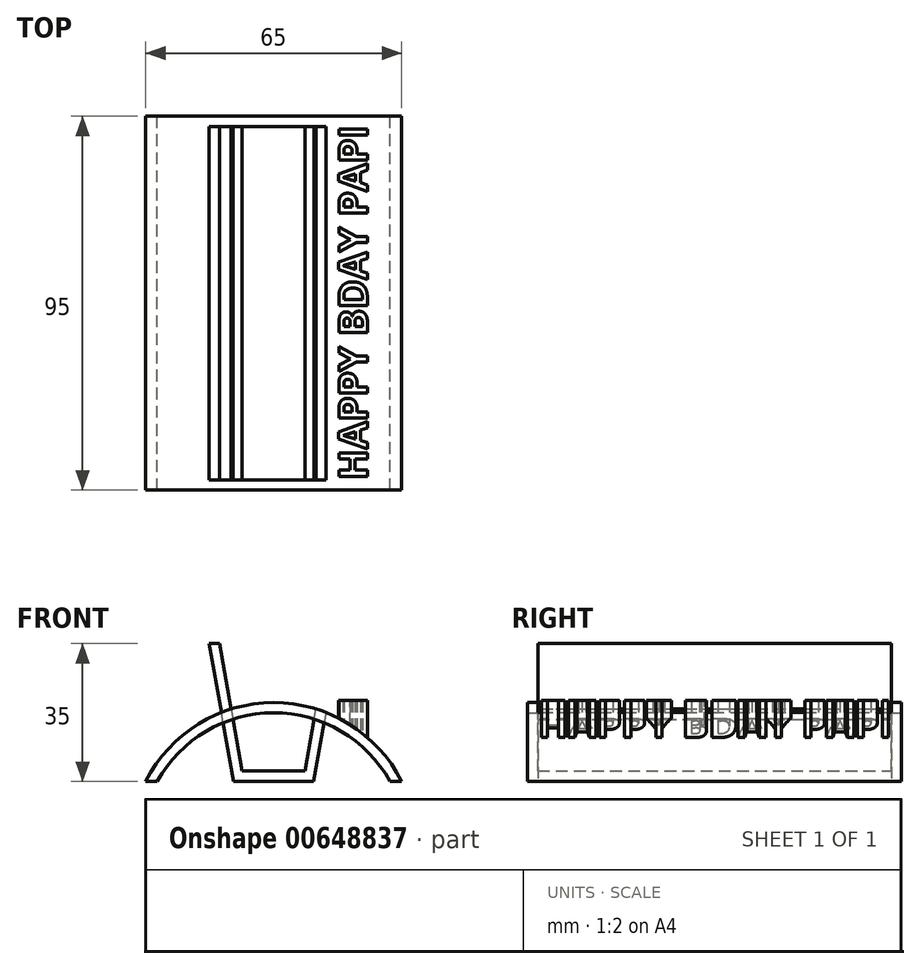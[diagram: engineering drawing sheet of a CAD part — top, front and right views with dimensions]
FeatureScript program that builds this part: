
annotation { "Feature Type Name" : "Feature", "Feature Type Description" : "" }
export const myFeature = defineFeature(function(context is Context, id is Id, definition is map)
    precondition{}
    {
        {
            var Q0;
            Q0=qCreatedBy(makeId("Front.planeOp"),FACE);
            var sketch = newSketch(context, id + "F0", { "sketchPlane" : qUnion([Q0])});
            skArc(sketch, "E0", {"start": v(32.5, 0) * mm, "mid": v(0, 20) * mm, "end": v(-32.5, 0) * mm});
            skLineSegment(sketch, "E1", {"start": v(-32.5, 0) * mm, "end": v(-29.56, 0) * mm});
            skArc(sketch, "E2", {"start": v(29.56, 0) * mm, "mid": v(0, 17.4) * mm, "end": v(-29.56, 0) * mm});
            skLineSegment(sketch, "E3", {"start": v(29.56, 0) * mm, "end": v(32.5, 0) * mm});
            skSolve(sketch);
        }
        {
            var Q0;
            Q0 = qSketchRegion(id + "F0", true);
            extrude(context, id + "F1", {"entities" : qUnion([Q0]), "endBound" : BoundingType.SYMMETRIC, "depth" : 95 * mm, "offsetDistance" : 25 * mm});
        }
        {
            var Q0;
            Q0=qCreatedBy(makeId("Front.planeOp"),FACE);
            var sketch = newSketch(context, id + "F2", { "sketchPlane" : qUnion([Q0])});
            skLineSegment(sketch, "E4", {"start": v(-13.71, 35) * mm, "end": v(-8, 2.6) * mm});
            skLineSegment(sketch, "E5", {"start": v(-8, 2.6) * mm, "end": v(8, 2.6) * mm});
            skLineSegment(sketch, "E6", {"start": v(8, 2.6) * mm, "end": v(10.78, 18.37) * mm});
            skLineSegment(sketch, "E7", {"start": v(13.27, 17.5) * mm, "end": v(10.18, 0) * mm});
            skLineSegment(sketch, "E8", {"start": v(10.18, 0) * mm, "end": v(-10.18, 0) * mm});
            skLineSegment(sketch, "E9", {"start": v(-10.18, 0) * mm, "end": v(-16.35, 35) * mm});
            skLineSegment(sketch, "E10", {"start": v(-16.35, 35) * mm, "end": v(-13.71, 35) * mm});
            skArc(sketch, "E11", {"start": v(13.27, 17.5) * mm, "mid": v(12.03, 17.95) * mm, "end": v(10.78, 18.37) * mm});
            skSolve(sketch);
        }
        {
            var Q0;
            Q0 = qSketchRegion(id + "F2", true);
            extrude(context, id + "F3", {"entities" : qUnion([Q0]), "endBound" : BoundingType.SYMMETRIC, "depth" : 89.8 * mm, "offsetDistance" : 25 * mm});
        }
        {
            var Q0;
            Q0=qCreatedBy(makeId("Front.planeOp"),FACE);
            var sketch = newSketch(context, id + "F4", { "sketchPlane" : qUnion([Q0])});
            skLineSegment(sketch, "E12", {"start": v(-11.77, 24) * mm, "end": v(-9.3, 10) * mm});
            skLineSegment(sketch, "E13", {"start": v(-9.3, 10) * mm, "end": v(9.3, 10) * mm});
            skLineSegment(sketch, "E14", {"start": v(-11.77, 24) * mm, "end": v(11.77, 24) * mm});
            skLineSegment(sketch, "E15", {"start": v(11.77, 24) * mm, "end": v(9.3, 10) * mm});
            skSolve(sketch);
        }
        {
            var Q0;
            Q0 = qSketchRegion(id + "F4", true);
            extrude(context, id + "F5", {"entities" : qUnion([Q0]), "endBound" : BoundingType.SYMMETRIC, "depth" : 89.8 * mm, "offsetDistance" : 25 * mm});
        }
        {
            var Q0;
            Q0=makeQuery(id+"F5.opExtrude","SWEPT_BODY",BODY,{"disambiguationData":[OSD([sQuery(id+"F4.wireOp",EDGE,"E12"),sQuery(id+"F4.wireOp",EDGE,"E13"),sQuery(id+"F4.wireOp",EDGE,"E14"),sQuery(id+"F4.wireOp",EDGE,"E15")])]});
            var Q1;
            Q1=makeQuery(id+"F1.opExtrude","SWEPT_BODY",BODY,{"disambiguationData":[OSD([sQuery(id+"F0.wireOp",EDGE,"E0"),sQuery(id+"F0.wireOp",EDGE,"E1"),sQuery(id+"F0.wireOp",EDGE,"E2"),sQuery(id+"F0.wireOp",EDGE,"E3")])]});
            booleanBodies(context, id + "F6", {"operationType" : BooleanOperationType.SUBTRACTION, "tools" : qUnion([Q0]), "targets" : qUnion([Q1])});
        }
        {
            var Q0;
            Q0=qCreatedBy(makeId("Top.planeOp"),FACE);
            var sketch = newSketch(context, id + "F7", { "sketchPlane" : qUnion([Q0])});
            skText(sketch, "E16", { "text": "HAPPY BDAY PAPI", "fontName": "OpenSans-Bold.ttf"});
            const initialGuessF7  = {"E16": [0.02382, -0.0449, 0, 1, 0.00732]};
            skSetInitialGuess(sketch, initialGuessF7);
            skSolve(sketch);
        }
        {
            var Q0;
            Q0 = qSketchRegion(id + "F7", true);
            var Q1;
            Q1=makeQuery(id+"F1.opExtrude","SWEPT_FACE",FACE,{"disambiguationData":[OSD([sQuery(id+"F0.wireOp",EDGE,"E2")])]});
            extrude(context, id + "F8", {"entities" : qUnion([Q0]), "operationType" : NewBodyOperationType.ADD, "depth" : 20.55 * mm, "offsetDistance" : 25 * mm, "hasSecondDirection" : true, "secondDirectionBound" : SecondDirectionBoundingType.UP_TO_SURFACE, "secondDirectionOppositeDirection" : false, "secondDirectionDepth" : 5 * mm, "secondDirectionBoundEntityFace" : qUnion([Q1])});
        }
    });
